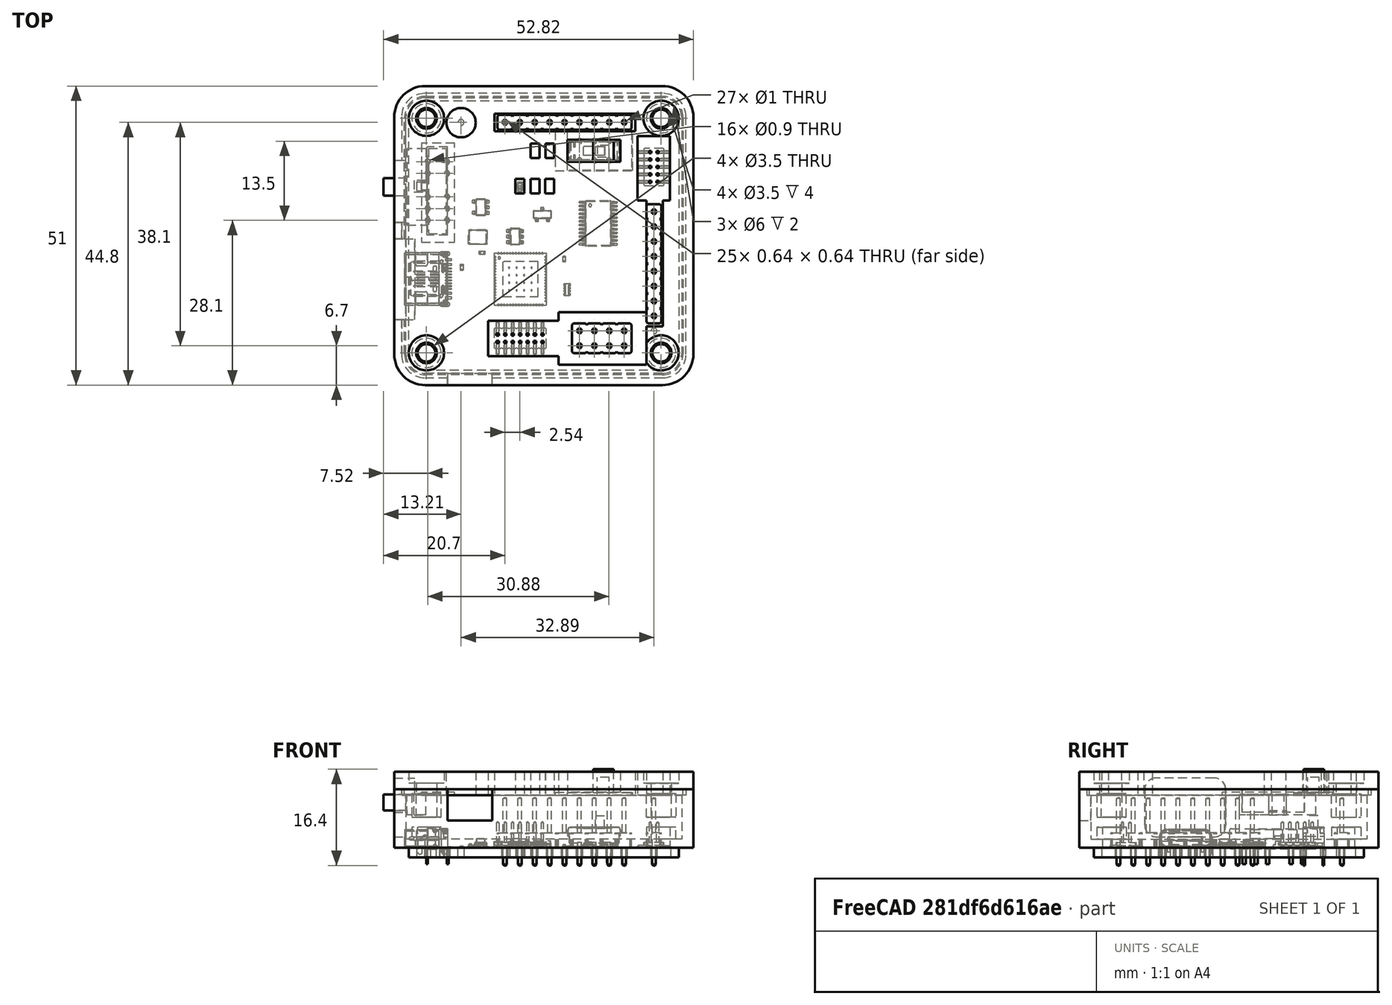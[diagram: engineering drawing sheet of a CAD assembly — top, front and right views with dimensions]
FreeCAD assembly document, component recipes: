
FREECAD ASSEMBLY — COMPONENT RECIPES ("TigarDen")

This assembly document has 73 components, labeled P0..P72 below (a component is one placed body or linked part). 11 of them carry a construction recipe — the FreeCAD feature program that regenerates the part from scratch, quoted from this document or its linked companion documents; the rest are supplied as boundary geometry only. No exploded tour is included for this assembly.
COMPONENT P0 — recipe-attached ("Body", modeled in this document).
Construction recipe (the document's own serialized feature program — sketch geometry with constraints, then the solid features built on it; lengths are millimeters unless a unit is written):

FEATURE [Sketcher::SketchObject] Sketch  label="Tikgard Sketch"
  AttachmentOffset = pos=(0,0,6) rot=(0,0,1;0rad)
  FullyConstrained = true
  MapMode = 5
  Placement = pos=(0,0,6) rot=(0,0,1;0rad)
  Support = -> [XY_Plane]
  sketch-geometry (8):
    g0: LineSegment StartX=-20.2 StartY=23.5 StartZ=0 EndX=20.2 EndY=23.5 EndZ=0
    g1: LineSegment StartX=23.5 StartY=20.2 StartZ=0 EndX=23.5 EndY=-20.2 EndZ=0
    g2: LineSegment StartX=20.2 StartY=-23.5 StartZ=0 EndX=-20.2 EndY=-23.5 EndZ=0
    g3: LineSegment StartX=-23.5 StartY=-20.2 StartZ=0 EndX=-23.5 EndY=20.2 EndZ=0
    g4: ArcOfCircle CenterX=-20.2 CenterY=20.2 CenterZ=0 NormalX=0 NormalY=0 NormalZ=1 AngleXU=0 Radius=3.3 StartAngle=1.5708 EndAngle=3.14159
    g5: ArcOfCircle CenterX=20.2 CenterY=20.2 CenterZ=0 NormalX=0 NormalY=0 NormalZ=1 AngleXU=0 Radius=3.3 StartAngle=0 EndAngle=1.5708
    g6: ArcOfCircle CenterX=20.2 CenterY=-20.2 CenterZ=0 NormalX=0 NormalY=0 NormalZ=1 AngleXU=0 Radius=3.3 StartAngle=4.71239 EndAngle=6.28319
    g7: ArcOfCircle CenterX=-20.2 CenterY=-20.2 CenterZ=0 NormalX=0 NormalY=0 NormalZ=1 AngleXU=0 Radius=3.3 StartAngle=3.14159 EndAngle=4.71239
  constraints (20):
    c: Horizontal(g0)
    c: Horizontal(g2)
    c: Vertical(g1)
    c: Vertical(g3)
    c: Distance(g-1,g2) = 23.5
    c: Distance(g-1,g3) = 23.5
    c: Tangent(g0,g4) = 1.5708
    c: Tangent(g3,g4) = 1.5708
    c: Tangent(g0,g5) = 1.5708
    c: Tangent(g1,g5) = 1.5708
    c: Tangent(g1,g6) = 1.5708
    c: Tangent(g2,g6) = 1.5708
    c: Tangent(g2,g7) = 1.5708
    c: Tangent(g3,g7) = 1.5708
    c: Radius(g4) = 3.3
    c: Radius(g6) = 3.3
    c: Radius(g7) = 3.3
    c: Distance(g3,g1) = 47
    c: Distance(g0,g2) = 47
    c: Radius(g5) = 3.3
FEATURE [Sketcher::SketchObject] Sketch001  label="Out Wall Sketch"
  FullyConstrained = true
  MapMode = 5
  Support = -> [XY_Plane]
  sketch-geometry (8):
    g0: LineSegment StartX=-20.2 StartY=25.5 StartZ=0 EndX=20.2 EndY=25.5 EndZ=0
    g1: LineSegment StartX=25.5 StartY=20.2 StartZ=0 EndX=25.5 EndY=-20.2 EndZ=0
    g2: LineSegment StartX=20.2 StartY=-25.5 StartZ=0 EndX=-20.2 EndY=-25.5 EndZ=0
    g3: LineSegment StartX=-25.5 StartY=-20.2 StartZ=0 EndX=-25.5 EndY=20.2 EndZ=0
    g4: ArcOfCircle CenterX=-20.2 CenterY=20.2 CenterZ=0 NormalX=0 NormalY=0 NormalZ=1 AngleXU=0 Radius=5.3 StartAngle=1.5708 EndAngle=3.14159
    g5: ArcOfCircle CenterX=-20.2 CenterY=-20.2 CenterZ=0 NormalX=0 NormalY=0 NormalZ=1 AngleXU=0 Radius=5.3 StartAngle=3.14159 EndAngle=4.71239
    g6: ArcOfCircle CenterX=20.2 CenterY=-20.2 CenterZ=0 NormalX=0 NormalY=0 NormalZ=1 AngleXU=0 Radius=5.3 StartAngle=4.71239 EndAngle=6.28319
    g7: ArcOfCircle CenterX=20.2 CenterY=20.2 CenterZ=0 NormalX=0 NormalY=0 NormalZ=1 AngleXU=0 Radius=5.3 StartAngle=1e-16 EndAngle=1.5708
  constraints (20):
    c: Horizontal(g0)
    c: Horizontal(g2)
    c: Vertical(g1)
    c: Vertical(g3)
    c: Tangent(g0,g4) = 1.5708
    c: Tangent(g3,g4) = 1.5708
    c: Tangent(g3,g5) = 1.5708
    c: Tangent(g2,g5) = 1.5708
    c: Tangent(g2,g6) = 1.5708
    c: Tangent(g1,g6) = 1.5708
    c: Tangent(g0,g7) = 1.5708
    c: Tangent(g1,g7) = 1.5708
    c: Radius(g4) = 5.3
    c: Radius(g7) = 5.3
    c: Radius(g6) = 5.3
    c: Radius(g5) = 5.3
    c: Distance(g0,g2) = 51
    c: Distance(g3,g1) = 51
    c: Distance(g-1,g0) = 25.5
    c: Distance(g-1,g1) = 25.5
FEATURE [PartDesign::Pad] Pad  label="Base"
  Direction = (1,1,1)
  Length = 10
  Length2 = 100
  Profile = -> Sketch001
  Type = 0
FEATURE [PartDesign::Pocket] Pocket  label="Tigard Cutout"
  BaseFeature = -> Pad
  Length = 9
  Length2 = 100
  Midplane = true
  Profile = -> Sketch
  Type = 0
FEATURE [Sketcher::SketchObject] Sketch002  label="Standoff Sketch"
  FullyConstrained = true
  MapMode = 5
  Placement = pos=(0,0,1.5) rot=(0,0,1;0rad)
  Support = -> [Pocket]
  sketch-geometry (4):
    g0: Circle CenterX=-20 CenterY=20 CenterZ=0 NormalX=0 NormalY=0 NormalZ=1 AngleXU=0 Radius=2.5
    g1: Circle CenterX=20 CenterY=20 CenterZ=0 NormalX=0 NormalY=0 NormalZ=1 AngleXU=0 Radius=2.5
    g2: Circle CenterX=20 CenterY=-20 CenterZ=0 NormalX=0 NormalY=0 NormalZ=1 AngleXU=0 Radius=2.5
    g3: Circle CenterX=-20 CenterY=-20 CenterZ=0 NormalX=0 NormalY=0 NormalZ=1 AngleXU=0 Radius=2.5
  constraints (12):
    c: Distance(g0,g-2) = 20
    c: Distance(g0,g-1) = 20
    c: Radius(g0) = 2.5
    c: Equal(g0,g1)
    c: Equal(g0,g3)
    c: Equal(g1,g2)
    c: DistanceX(g-2,g1) = 20
    c: DistanceY(g-1,g1) = 20
    c: DistanceY(g-1,g2) = -20
    c: DistanceX(g-2,g2) = 20
    c: DistanceX(g-2,g3) = -20
    c: DistanceY(g-1,g3) = -20
FEATURE [Sketcher::SketchObject] Sketch003  label="Screw Holes Sketch"
  FullyConstrained = true
  MapMode = 5
  Placement = pos=(0,0,3.5) rot=(0,0,1;0rad)
  sketch-geometry (4):
    g0: Circle CenterX=-20 CenterY=20 CenterZ=0 NormalX=0 NormalY=0 NormalZ=1 AngleXU=0 Radius=1.5
    g1: Circle CenterX=20 CenterY=20 CenterZ=0 NormalX=0 NormalY=0 NormalZ=1 AngleXU=0 Radius=1.5
    g2: Circle CenterX=20 CenterY=-20 CenterZ=0 NormalX=0 NormalY=0 NormalZ=1 AngleXU=0 Radius=1.5
    g3: Circle CenterX=-20 CenterY=-20 CenterZ=0 NormalX=0 NormalY=0 NormalZ=1 AngleXU=0 Radius=1.5
  constraints (12):
    c: DistanceX(g-2,g0) = -20
    c: Distance(g0,g-1) = 20
    c: Radius(g0) = 1.5
    c: Equal(g0,g1)
    c: Equal(g0,g2)
    c: Equal(g3,g2)
    c: Distance(g3,g-1) = 20
    c: Distance(g3,g-2) = 20
    c: Distance(g2,g-2) = 20
    c: Distance(g2,g-1) = 20
    c: Distance(g1,g-2) = 20
    c: Distance(g1,g-1) = 20
FEATURE [Sketcher::SketchObject] Sketch004  label="Base Ridge Sketch"
  FullyConstrained = true
  MapMode = 5
  Placement = pos=(0,0,10) rot=(0,0,1;0rad)
  Support = -> [Pocket]
  sketch-geometry (8):
    g0: LineSegment StartX=-20.25 StartY=24.25 StartZ=0 EndX=20.25 EndY=24.25 EndZ=0
    g1: LineSegment StartX=24.25 StartY=20.25 StartZ=0 EndX=24.25 EndY=-20.25 EndZ=0
    g2: LineSegment StartX=20.25 StartY=-24.25 StartZ=0 EndX=-20.25 EndY=-24.25 EndZ=0
    g3: LineSegment StartX=-24.25 StartY=-20.25 StartZ=0 EndX=-24.25 EndY=20.25 EndZ=0
    g4: ArcOfCircle CenterX=-20.25 CenterY=20.25 CenterZ=0 NormalX=0 NormalY=0 NormalZ=1 AngleXU=0 Radius=4 StartAngle=1.5708 EndAngle=3.14159
    g5: ArcOfCircle CenterX=20.25 CenterY=20.25 CenterZ=0 NormalX=0 NormalY=0 NormalZ=1 AngleXU=0 Radius=4 StartAngle=0 EndAngle=1.5708
    g6: ArcOfCircle CenterX=20.25 CenterY=-20.25 CenterZ=0 NormalX=0 NormalY=0 NormalZ=1 AngleXU=0 Radius=4 StartAngle=4.71239 EndAngle=6.28319
    g7: ArcOfCircle CenterX=-20.25 CenterY=-20.25 CenterZ=0 NormalX=0 NormalY=0 NormalZ=1 AngleXU=0 Radius=4 StartAngle=3.14159 EndAngle=4.71239
  constraints (20):
    c: Horizontal(g0)
    c: Horizontal(g2)
    c: Vertical(g1)
    c: Vertical(g3)
    c: Distance(g-1,g2) = 24.25
    c: Distance(g-1,g1) = 24.25
    c: Distance(g-1,g0) = 24.25
    c: Distance(g-1,g3) = 24.25
    c: Tangent(g0,g4) = 1.5708
    c: Tangent(g3,g4) = 1.5708
    c: Tangent(g0,g5) = 1.5708
    c: Tangent(g1,g5) = 1.5708
    c: Tangent(g1,g6) = 1.5708
    c: Tangent(g2,g6) = 1.5708
    c: Tangent(g2,g7) = 1.5708
    c: Tangent(g3,g7) = 1.5708
    c: Radius(g4) = 4
    c: Equal(g4,g5)
    c: Equal(g6,g4)
    c: Equal(g7,g4)
FEATURE [PartDesign::Pocket] Pocket001  label="Base Ridge"
  BaseFeature = -> Pocket
  Length = 2
  Length2 = 100
  Midplane = true
  Profile = -> Sketch004
  Type = 0
FEATURE [PartDesign::Pad] Pad004  label="Standoff"
  BaseFeature = -> Pocket001
  Direction = (1,1,1)
  Length = 2
  Length2 = 100
  Profile = -> Sketch002
  Type = 0
FEATURE [PartDesign::Pocket] Pocket002  label="Screw Holes"
  BaseFeature = -> Pad004
  Length = 5
  Length2 = 100
  Profile = -> Sketch003
  Type = 1
FEATURE [PartDesign::Body] Body
  Group = -> [Sketch,Sketch001,Pad,Pocket,Sketch002,Sketch003,Sketch004,Pocket001,Pad004,Pocket002]
  Origin = -> Origin
  Tip = -> Pocket002
COMPONENT P1 — recipe-attached ("Top", modeled in this document).
Construction recipe (the document's own serialized feature program — sketch geometry with constraints, then the solid features built on it; lengths are millimeters unless a unit is written):

FEATURE [Sketcher::SketchObject] Sketch005  label="Lid Inset Sketch"
  AttachmentOffset = pos=(0,0,7) rot=(0,0,1;0rad)
  FullyConstrained = true
  MapMode = 5
  Placement = pos=(0,0,7) rot=(0,0,1;0rad)
  Support = -> [XY_Plane001]
  sketch-geometry (8):
    g0: LineSegment StartX=-20.15 StartY=23.75 StartZ=0 EndX=20.15 EndY=23.75 EndZ=0
    g1: LineSegment StartX=23.75 StartY=20.15 StartZ=0 EndX=23.75 EndY=-20.15 EndZ=0
    g2: LineSegment StartX=20.15 StartY=-23.75 StartZ=0 EndX=-20.15 EndY=-23.75 EndZ=0
    g3: LineSegment StartX=-23.75 StartY=-20.15 StartZ=0 EndX=-23.75 EndY=20.15 EndZ=0
    g4: ArcOfCircle CenterX=-20.15 CenterY=20.15 CenterZ=0 NormalX=0 NormalY=0 NormalZ=1 AngleXU=0 Radius=3.6 StartAngle=1.5708 EndAngle=3.14159
    g5: ArcOfCircle CenterX=20.15 CenterY=20.15 CenterZ=0 NormalX=0 NormalY=0 NormalZ=1 AngleXU=0 Radius=3.6 StartAngle=2e-16 EndAngle=1.5708
    g6: ArcOfCircle CenterX=20.15 CenterY=-20.15 CenterZ=0 NormalX=0 NormalY=0 NormalZ=1 AngleXU=0 Radius=3.6 StartAngle=4.71239 EndAngle=6.28319
    g7: ArcOfCircle CenterX=-20.15 CenterY=-20.15 CenterZ=0 NormalX=0 NormalY=0 NormalZ=1 AngleXU=0 Radius=3.6 StartAngle=3.14159 EndAngle=4.71239
  constraints (20):
    c: Horizontal(g0)
    c: Horizontal(g2)
    c: Vertical(g1)
    c: Vertical(g3)
    c: Distance(g-1,g0) = 23.75
    c: Distance(g-1,g2) = 23.75
    c: Distance(g-1,g1) = 23.75
    c: Distance(g-1,g3) = 23.75
    c: Tangent(g0,g4) = 1.5708
    c: Tangent(g3,g4) = 1.5708
    c: Tangent(g0,g5) = 1.5708
    c: Tangent(g1,g5) = 1.5708
    c: Tangent(g1,g6) = 1.5708
    c: Tangent(g2,g6) = 1.5708
    c: Tangent(g2,g7) = 1.5708
    c: Tangent(g3,g7) = 1.5708
    c: Radius(g4) = 3.6
    c: Equal(g4,g5)
    c: Equal(g6,g4)
    c: Equal(g4,g7)
FEATURE [PartDesign::Pad] Pad002  label="Lid Inset"
  Direction = (1,1,1)
  Length = 1
  Length2 = 100
  Profile = -> Sketch005
  Type = 0
FEATURE [Sketcher::SketchObject] Sketch006  label="Lid Sketch"
  FullyConstrained = true
  MapMode = 5
  Placement = pos=(0,0,8) rot=(0,0,1;0rad)
  Support = -> [Pad002]
  sketch-geometry (8):
    g0: LineSegment StartX=-20.2 StartY=25.5 StartZ=0 EndX=20.2 EndY=25.5 EndZ=0
    g1: LineSegment StartX=25.5 StartY=20.2 StartZ=0 EndX=25.5 EndY=-20.2 EndZ=0
    g2: LineSegment StartX=20.2 StartY=-25.5 StartZ=0 EndX=-20.2 EndY=-25.5 EndZ=0
    g3: LineSegment StartX=-25.5 StartY=-20.2 StartZ=0 EndX=-25.5 EndY=20.2 EndZ=0
    g4: ArcOfCircle CenterX=-20.2 CenterY=20.2 CenterZ=0 NormalX=0 NormalY=0 NormalZ=1 AngleXU=0 Radius=5.3 StartAngle=1.5708 EndAngle=3.14159
    g5: ArcOfCircle CenterX=20.2 CenterY=20.2 CenterZ=0 NormalX=0 NormalY=0 NormalZ=1 AngleXU=0 Radius=5.3 StartAngle=1e-16 EndAngle=1.5708
    g6: ArcOfCircle CenterX=20.2 CenterY=-20.2 CenterZ=0 NormalX=0 NormalY=0 NormalZ=1 AngleXU=0 Radius=5.3 StartAngle=4.71239 EndAngle=6.28319
    g7: ArcOfCircle CenterX=-20.2 CenterY=-20.2 CenterZ=0 NormalX=0 NormalY=0 NormalZ=1 AngleXU=0 Radius=5.3 StartAngle=3.14159 EndAngle=4.71239
  constraints (20):
    c: Horizontal(g0)
    c: Horizontal(g2)
    c: Vertical(g1)
    c: Vertical(g3)
    c: Distance(g-1,g0) = 25.5
    c: Distance(g-1,g1) = 25.5
    c: Distance(g-1,g2) = 25.5
    c: Distance(g-1,g3) = 25.5
    c: Tangent(g0,g4) = 1.5708
    c: Tangent(g3,g4) = 1.5708
    c: Radius(g4) = 5.3
    c: Tangent(g0,g5) = 1.5708
    c: Tangent(g1,g5) = 1.5708
    c: Tangent(g1,g6) = 1.5708
    c: Tangent(g2,g6) = 1.5708
    c: Tangent(g2,g7) = 1.5708
    c: Tangent(g3,g7) = 1.5708
    c: Equal(g4,g5)
    c: Equal(g4,g6)
    c: Equal(g4,g7)
FEATURE [PartDesign::Pad] Pad003  label="Lid"
  BaseFeature = -> Pad002
  Direction = (1,1,1)
  Length = 3
  Length2 = 100
  Profile = -> Sketch006
  Type = 0
FEATURE [Sketcher::SketchObject] Sketch007  label="Screw Holes Lid"
  FullyConstrained = true
  MapMode = 5
  Placement = pos=(0,0,11) rot=(0,0,1;0rad)
  Support = -> [Pad003]
  sketch-geometry (4):
    g0: Circle CenterX=-20 CenterY=20 CenterZ=0 NormalX=0 NormalY=0 NormalZ=1 AngleXU=0 Radius=1.5
    g1: Circle CenterX=20 CenterY=20 CenterZ=0 NormalX=0 NormalY=0 NormalZ=1 AngleXU=0 Radius=1.5
    g2: Circle CenterX=20 CenterY=-20 CenterZ=0 NormalX=0 NormalY=0 NormalZ=1 AngleXU=0 Radius=1.5
    g3: Circle CenterX=-20 CenterY=-20 CenterZ=0 NormalX=0 NormalY=0 NormalZ=1 AngleXU=0 Radius=1.5
  constraints (12):
    c: Radius(g0) = 1.5
    c: DistanceX(g-2,g0) = -20
    c: DistanceY(g-1,g0) = 20
    c: Equal(g0,g1)
    c: Equal(g0,g2)
    c: Equal(g0,g3)
    c: DistanceX(g-2,g1) = 20
    c: DistanceY(g-1,g1) = 20
    c: DistanceX(g-2,g2) = 20
    c: DistanceY(g-1,g2) = -20
    c: DistanceX(g-2,g3) = -20
    c: DistanceY(g-1,g3) = -20
FEATURE [PartDesign::Hole] Hole
  BaseFeature = -> Pad003
  Depth = 25
  DepthType = 1
  Diameter = 3.5
  DrillForDepth = true
  DrillPoint = 1
  DrillPointAngle = 118
  HoleCutCountersinkAngle = 90
  HoleCutCustomValues = false
  HoleCutDepth = 2
  HoleCutDiameter = 6
  HoleCutType = 1
  ModelActualThread = false
  Profile = -> Sketch007
  Tapered = false
  TaperedAngle = 90
  ThreadAngle = 0
  ThreadClass = 0
  ThreadCutOffInner = 0
  ThreadCutOffOuter = 0
  ThreadDirection = 0
  ThreadFit = 0
  ThreadPitch = 0
  ThreadSize = 0
  ThreadType = 0
  Threaded = false
FEATURE [PartDesign::Body] Body001  label="Top"
  Group = -> [Sketch005,Pad002,Sketch006,Pad003,Sketch007,Hole]
  Origin = -> Origin001
  Placement = pos=(0,0,2) rot=(0,0,1;0rad)
  Tip = -> Hole
COMPONENT P2 — recipe-attached ("USB-C Cutter", modeled in this document).
Construction recipe (the document's own serialized feature program — sketch geometry with constraints, then the solid features built on it; lengths are millimeters unless a unit is written):

FEATURE [Sketcher::SketchObject] Sketch008
  FullyConstrained = false
  MapMode = 5
  Placement = pos=(0,0,0) rot=(-0.57735,0.57735,0.57735;4.18879rad)
  Support = -> [YZ_Plane002]
  sketch-geometry (8):
    g0: LineSegment StartX=2.5358 StartY=11.912 StartZ=0 EndX=12.3476 EndY=11.912 EndZ=0
    g1: LineSegment StartX=14.3476 StartY=9.91198 StartZ=0 EndX=14.3476 EndY=3.8669 EndZ=0
    g2: LineSegment StartX=12.3476 StartY=1.8669 StartZ=0 EndX=2.5358 EndY=1.8669 EndZ=0
    g3: LineSegment StartX=0.535801 StartY=3.8669 StartZ=0 EndX=0.535801 EndY=9.91198 EndZ=0
    g4: ArcOfCircle CenterX=2.5358 CenterY=9.91198 CenterZ=0 NormalX=0 NormalY=0 NormalZ=1 AngleXU=0 Radius=2 StartAngle=1.5708 EndAngle=3.14159
    g5: ArcOfCircle CenterX=12.3476 CenterY=9.91198 CenterZ=0 NormalX=0 NormalY=0 NormalZ=1 AngleXU=0 Radius=2 StartAngle=0 EndAngle=1.5708
    g6: ArcOfCircle CenterX=12.3476 CenterY=3.8669 CenterZ=0 NormalX=0 NormalY=0 NormalZ=1 AngleXU=0 Radius=2 StartAngle=4.71239 EndAngle=6.28319
    g7: ArcOfCircle CenterX=2.5358 CenterY=3.8669 CenterZ=0 NormalX=0 NormalY=0 NormalZ=1 AngleXU=0 Radius=2 StartAngle=3.14159 EndAngle=4.71239
  constraints (16):
    c: Horizontal(g0)
    c: Horizontal(g2)
    c: Vertical(g1)
    c: Vertical(g3)
    c: Tangent(g3,g4) = 1.5708
    c: Tangent(g0,g4) = 1.5708
    c: Tangent(g0,g5) = 1.5708
    c: Tangent(g1,g5) = 1.5708
    c: Tangent(g1,g6) = 1.5708
    c: Tangent(g2,g6) = 1.5708
    c: Tangent(g2,g7) = 1.5708
    c: Tangent(g3,g7) = 1.5708
    c: Radius(g4) = 2
    c: Equal(g4,g5)
    c: Equal(g4,g7)
    c: Equal(g4,g6)
FEATURE [PartDesign::Pad] Pad005
  Direction = (1,1,1)
  Length = 4
  Length2 = 100
  Placement = pos=(0,0,0) rot=(0.57735,0.57735,0.57735;2.0944rad)
  Profile = -> Sketch008
  Reversed = true
  Type = 0
FEATURE [PartDesign::Body] Body002  label="USB-C Cutter"
  Group = -> [Sketch008,Pad005]
  Origin = -> Origin002
  Placement = pos=(-26,0,0) rot=(0,0,1;0rad)
  Tip = -> Pad005
COMPONENT P3 — recipe-attached ("Body Pocketed", modeled in this document).
Construction recipe (the document's own serialized feature program — sketch geometry with constraints, then the solid features built on it; lengths are millimeters unless a unit is written):

FEATURE [PartDesign::FeatureBase] BaseFeature
  BaseFeature = -> Cut001
FEATURE [Sketcher::SketchObject] Sketch009  label="Voltage Switch Cutout Sketch"
  FullyConstrained = false
  MapMode = 5
  Placement = pos=(-25.5,0,0) rot=(0.57735,-0.57735,-0.57735;2.0944rad)
  Support = -> [BaseFeature]
  sketch-geometry (4):
    g0: LineSegment StartX=-12.842 StartY=6.08226 StartZ=0 EndX=-2.23477 EndY=6.08226 EndZ=0
    g1: LineSegment StartX=-2.23477 StartY=6.08226 StartZ=0 EndX=-2.23477 EndY=10.517 EndZ=0
    g2: LineSegment StartX=-2.23477 StartY=10.517 StartZ=0 EndX=-12.842 EndY=10.517 EndZ=0
    g3: LineSegment StartX=-12.842 StartY=10.517 StartZ=0 EndX=-12.842 EndY=6.08226 EndZ=0
  constraints (8):
    c: Coincident(g0,g1)
    c: Coincident(g1,g2)
    c: Coincident(g2,g3)
    c: Coincident(g3,g0)
    c: Horizontal(g0)
    c: Horizontal(g2)
    c: Vertical(g1)
    c: Vertical(g3)
FEATURE [PartDesign::Pocket] Pocket003  label="Voltage Switch Cutout"
  BaseFeature = -> BaseFeature
  Length = 5
  Length2 = 100
  Placement = pos=(0,0,-40) rot=(0,0,1;0rad)
  Profile = -> Sketch009
  Type = 0
FEATURE [Sketcher::SketchObject] Sketch010  label="I2C Cutout Sketch"
  FullyConstrained = false
  MapMode = 5
  Placement = pos=(0,-25.5,0) rot=(1,0,0;1.5708rad)
  Support = -> [Pocket003]
  sketch-geometry (4):
    g0: LineSegment StartX=-8.76633 StartY=4.68576 StartZ=0 EndX=-16.4093 EndY=4.68576 EndZ=0
    g1: LineSegment StartX=-16.4093 StartY=4.68576 StartZ=0 EndX=-16.4093 EndY=10.0143 EndZ=0
    g2: LineSegment StartX=-16.4093 StartY=10.0143 StartZ=0 EndX=-8.76633 EndY=10.0143 EndZ=0
    g3: LineSegment StartX=-8.76633 StartY=10.0143 StartZ=0 EndX=-8.76633 EndY=4.68576 EndZ=0
  constraints (8):
    c: Coincident(g0,g1)
    c: Coincident(g1,g2)
    c: Coincident(g2,g3)
    c: Coincident(g3,g0)
    c: Horizontal(g0)
    c: Horizontal(g2)
    c: Vertical(g1)
    c: Vertical(g3)
FEATURE [PartDesign::Pocket] Pocket004  label="I2C Cutout"
  BaseFeature = -> Pocket003
  Length = 5
  Length2 = 100
  Profile = -> Sketch010
  Type = 0
FEATURE [PartDesign::Body] Body003  label="Body Pocketed"
  BaseFeature = -> Cut001
  Group = -> [BaseFeature,Sketch009,Pocket003,Sketch010,Pocket004]
  Origin = -> Origin003
  Tip = -> Pocket004
COMPONENT P4 — recipe-attached ("Lid Pocketed", modeled in this document).
Construction recipe (the document's own serialized feature program — sketch geometry with constraints, then the solid features built on it; lengths are millimeters unless a unit is written):

FEATURE [PartDesign::FeatureBase] BaseFeature001
  BaseFeature = -> Cut
FEATURE [Sketcher::SketchObject] Sketch011  label="Lid Cutout Sketch"
  FullyConstrained = false
  MapMode = 5
  Placement = pos=(0,0,13) rot=(0,0,1;0rad)
  Support = -> [BaseFeature001]
  sketch-geometry (45):
    g0: LineSegment StartX=4.02651 StartY=16.3347 StartZ=0 EndX=13.0689 EndY=16.3347 EndZ=0
    g1: LineSegment StartX=13.0689 StartY=16.3347 StartZ=0 EndX=13.0689 EndY=12.5671 EndZ=0
    g2: LineSegment StartX=13.0689 StartY=12.5671 StartZ=0 EndX=4.02651 EndY=12.5671 EndZ=0
    g3: LineSegment StartX=4.02651 StartY=12.5671 StartZ=0 EndX=4.02651 EndY=16.3347 EndZ=0
    g4: LineSegment StartX=15.9986 StartY=16.9943 StartZ=0 EndX=21.4986 EndY=16.9943 EndZ=0
    g5: LineSegment StartX=21.4986 StartY=16.9943 StartZ=0 EndX=21.4986 EndY=5.99431 EndZ=0
    g6: LineSegment StartX=15.9986 StartY=5.99431 StartZ=0 EndX=15.9986 EndY=16.9943 EndZ=0
    g7: LineSegment StartX=20.2805 StartY=5.99431 StartZ=0 EndX=20.2805 EndY=-15.5057 EndZ=0
    g8: LineSegment StartX=20.2805 StartY=-15.5057 StartZ=0 EndX=17.5 EndY=-15.5057 EndZ=0
    g9: LineSegment StartX=17.5 StartY=-13.0474 StartZ=0 EndX=17.5 EndY=5.99431 EndZ=0
    g10: LineSegment StartX=-8.41441 StartY=20.8038 StartZ=0 EndX=15.5856 EndY=20.8038 EndZ=0
    g11: LineSegment StartX=15.5856 StartY=20.8038 StartZ=0 EndX=15.5856 EndY=17.8038 EndZ=0
    g12: LineSegment StartX=15.5856 StartY=17.8038 StartZ=0 EndX=-8.41441 EndY=17.8038 EndZ=0
    g13: LineSegment StartX=-8.41441 StartY=17.8038 StartZ=0 EndX=-8.41441 EndY=20.8038 EndZ=0
    g14: LineSegment StartX=15.9986 StartY=5.99431 StartZ=0 EndX=17.5 EndY=5.99431 EndZ=0
    g15: LineSegment StartX=20.2805 StartY=5.99431 StartZ=0 EndX=21.4986 EndY=5.99431 EndZ=0
    g16: LineSegment StartX=-2.2549 StartY=15.7 StartZ=0 EndX=-0.754905 EndY=15.7 EndZ=0
    g17: LineSegment StartX=-0.754905 StartY=15.7 StartZ=0 EndX=-0.754905 EndY=13.2 EndZ=0
    g18: LineSegment StartX=-0.754905 StartY=13.2 StartZ=0 EndX=-2.2549 EndY=13.2 EndZ=0
    g19: LineSegment StartX=-2.2549 StartY=13.2 StartZ=0 EndX=-2.2549 EndY=15.7 EndZ=0
    g20: LineSegment StartX=0.270606 StartY=15.7 StartZ=0 EndX=1.77061 EndY=15.7 EndZ=0
    g21: LineSegment StartX=1.77061 StartY=15.7 StartZ=0 EndX=1.77061 EndY=13.2 EndZ=0
    g22: LineSegment StartX=1.77061 StartY=13.2 StartZ=0 EndX=0.270606 EndY=13.2 EndZ=0
    g23: LineSegment StartX=0.270606 StartY=13.2 StartZ=0 EndX=0.270606 EndY=15.7 EndZ=0
    g24: LineSegment StartX=0.239071 StartY=9.7 StartZ=0 EndX=1.73907 EndY=9.7 EndZ=0
    g25: LineSegment StartX=1.73907 StartY=9.7 StartZ=0 EndX=1.73907 EndY=7.2 EndZ=0
    g26: LineSegment StartX=1.73907 StartY=7.2 StartZ=0 EndX=0.239071 EndY=7.2 EndZ=0
    g27: LineSegment StartX=0.239071 StartY=7.2 StartZ=0 EndX=0.239071 EndY=9.7 EndZ=0
    g28: LineSegment StartX=-2.24916 StartY=9.7 StartZ=0 EndX=-0.749158 EndY=9.7 EndZ=0
    g29: LineSegment StartX=-0.749158 StartY=9.7 StartZ=0 EndX=-0.749158 EndY=7.2 EndZ=0
    g30: LineSegment StartX=-0.749158 StartY=7.2 StartZ=0 EndX=-2.24916 EndY=7.2 EndZ=0
    g31: LineSegment StartX=-2.24916 StartY=7.2 StartZ=0 EndX=-2.24916 EndY=9.7 EndZ=0
    g32: LineSegment StartX=-4.81914 StartY=9.7 StartZ=0 EndX=-3.31914 EndY=9.7 EndZ=0
    g33: LineSegment StartX=-3.31914 StartY=9.7 StartZ=0 EndX=-3.31914 EndY=7.2 EndZ=0
    g34: LineSegment StartX=-3.31914 StartY=7.2 StartZ=0 EndX=-4.81914 EndY=7.2 EndZ=0
    g35: LineSegment StartX=-4.81914 StartY=7.2 StartZ=0 EndX=-4.81914 EndY=9.7 EndZ=0
    g36: LineSegment StartX=-9.5 StartY=-14.5357 StartZ=0 EndX=2.5 EndY=-14.5357 EndZ=0
    g37: LineSegment StartX=2.5 StartY=-20.5357 StartZ=0 EndX=-9.5 EndY=-20.5357 EndZ=0
    g38: LineSegment StartX=-9.5 StartY=-20.5357 StartZ=0 EndX=-9.5 EndY=-14.5357 EndZ=0
    g39: LineSegment StartX=2.5 StartY=-13.0474 StartZ=0 EndX=17.5 EndY=-13.0474 EndZ=0
    g40: LineSegment StartX=17.5 StartY=-15.5057 StartZ=0 EndX=17.5 EndY=-22.0474 EndZ=0
    g41: LineSegment StartX=17.5 StartY=-22.0474 StartZ=0 EndX=2.5 EndY=-22.0474 EndZ=0
    g42: LineSegment StartX=2.5 StartY=-22.0474 StartZ=0 EndX=2.5 EndY=-20.5357 EndZ=0
    g43: LineSegment StartX=2.5 StartY=-14.5357 StartZ=0 EndX=2.5 EndY=-13.0474 EndZ=0
    g44: Circle CenterX=-14.1023 CenterY=19.26 CenterZ=0 NormalX=0 NormalY=0 NormalZ=1 AngleXU=0 Radius=2.5
  constraints (115):
    c: Coincident(g0,g1)
    c: Coincident(g1,g2)
    c: Coincident(g2,g3)
    c: Coincident(g3,g0)
    c: Horizontal(g0)
    c: Horizontal(g2)
    c: Vertical(g1)
    c: Vertical(g3)
    c: Coincident(g4,g5)
    c: Coincident(g6,g4)
    c: Horizontal(g4)
    c: Vertical(g5)
    c: Vertical(g6)
    c: Coincident(g7,g8)
    c: Horizontal(g8)
    c: Vertical(g7)
    c: Vertical(g9)
    c: Distance(g7) = 21.5
    c: Coincident(g10,g11)
    c: Coincident(g11,g12)
    c: Coincident(g12,g13)
    c: Coincident(g13,g10)
    c: Horizontal(g10)
    c: Horizontal(g12)
    c: Vertical(g11)
    c: Vertical(g13)
    c: Distance(g10) = 24
    c: Distance(g13) = 3
    c: Distance(g4) = 5.5
    c: Coincident(g14,g6)
    c: Coincident(g14,g9)
    c: Horizontal(g14)
    c: Coincident(g15,g7)
    c: Coincident(g15,g5)
    c: Horizontal(g15)
    c: Distance(g5) = 11
    c: Equal(g5,g6)
    c: Coincident(g16,g17)
    c: Coincident(g17,g18)
    c: Coincident(g18,g19)
    c: Coincident(g19,g16)
    c: Horizontal(g16)
    c: Horizontal(g18)
    c: Vertical(g17)
    c: Vertical(g19)
    c: Coincident(g20,g21)
    c: Coincident(g21,g22)
    c: Coincident(g22,g23)
    c: Coincident(g23,g20)
    c: Horizontal(g20)
    c: Horizontal(g22)
    c: Vertical(g21)
    c: Vertical(g23)
    c: Coincident(g24,g25)
    c: Coincident(g25,g26)
    c: Coincident(g26,g27)
    c: Coincident(g27,g24)
    c: Horizontal(g24)
    c: Horizontal(g26)
    c: Vertical(g25)
    c: Vertical(g27)
    c: Coincident(g28,g29)
    c: Coincident(g29,g30)
    c: Coincident(g30,g31)
    c: Coincident(g31,g28)
    c: Horizontal(g28)
    c: Horizontal(g30)
    c: Vertical(g29)
    c: Vertical(g31)
    c: Coincident(g32,g33)
    c: Coincident(g33,g34)
    c: Coincident(g34,g35)
    c: Coincident(g35,g32)
    c: Horizontal(g32)
    c: Horizontal(g34)
    c: Vertical(g33)
    c: Vertical(g35)
    c: Coincident(g37,g38)
    c: Coincident(g38,g36)
    c: Horizontal(g36)
    c: Horizontal(g37)
    c: Vertical(g38)
    c: Distance(g36) = 12
    c: Distance(g38) = 6
    c: Coincident(g40,g41)
    c: Coincident(g41,g42)
    c: Coincident(g43,g39)
    c: Horizontal(g39)
    c: Horizontal(g41)
    c: Vertical(g40)
    c: Vertical(g42)
    c: Distance(g39) = 15
    c: Coincident(g42,g37)
    c: Coincident(g43,g36)
    c: Tangent(g42,g43)
    c: Distance(g19) = 2.5
    c: Distance(g16) = 1.5
    c: Equal(g19,g23)
    c: Equal(g16,g20)
    c: Equal(g16,g28)
    c: Equal(g19,g31)
    c: Equal(g31,g27)
    c: Equal(g31,g35)
    c: Equal(g18,g32)
    c: Equal(g18,g24)
    c: Distance(g-1,g34) = 7.2
    c: Distance(g-1,g26) = 7.2
    c: Distance(g-1,g30) = 7.2
    c: Distance(g-1,g18) = 13.2
    c: Distance(g-1,g22) = 13.2
    c: Radius(g44) = 2.5
    c: Distance(g-1,g40) = 17.5
    c: Coincident(g9,g39)
    c: PointOnObject(g40,g8)
    c: DistanceX(g-2,g39) = 2.5
FEATURE [PartDesign::Pocket] Pocket005  label="Lid Cutouts"
  BaseFeature = -> BaseFeature001
  Length = 5
  Length2 = 100
  Profile = -> Sketch011
  Type = 0
FEATURE [Sketcher::SketchObject] Sketch012  label="Switch-Lid Indent Sketch"
  FullyConstrained = false
  MapMode = 5
  Placement = pos=(0,0,9) rot=(1,0,0;3.14159rad)
  Support = -> [Pocket005]
  sketch-geometry (8):
    g0: LineSegment StartX=-20.8484 StartY=1.12147 StartZ=0 EndX=-15.2184 EndY=1.12147 EndZ=0
    g1: LineSegment StartX=-15.2184 StartY=1.12147 StartZ=0 EndX=-15.2184 EndY=-15.7685 EndZ=0
    g2: LineSegment StartX=-15.2184 StartY=-15.7685 StartZ=0 EndX=-20.8484 EndY=-15.7685 EndZ=0
    g3: LineSegment StartX=-20.8484 StartY=-15.7685 StartZ=0 EndX=-20.8484 EndY=1.12147 EndZ=0
    g4: LineSegment StartX=1.95221 StartY=-11.0754 StartZ=0 EndX=15.1288 EndY=-11.0754 EndZ=0
    g5: LineSegment StartX=15.1288 StartY=-11.0754 StartZ=0 EndX=15.1288 EndY=-18.1428 EndZ=0
    g6: LineSegment StartX=15.1288 StartY=-18.1428 StartZ=0 EndX=1.95221 EndY=-18.1428 EndZ=0
    g7: LineSegment StartX=1.95221 StartY=-18.1428 StartZ=0 EndX=1.95221 EndY=-11.0754 EndZ=0
  constraints (16):
    c: Coincident(g0,g1)
    c: Coincident(g1,g2)
    c: Coincident(g2,g3)
    c: Coincident(g3,g0)
    c: Horizontal(g0)
    c: Horizontal(g2)
    c: Vertical(g1)
    c: Vertical(g3)
    c: Coincident(g4,g5)
    c: Coincident(g5,g6)
    c: Coincident(g6,g7)
    c: Coincident(g7,g4)
    c: Horizontal(g4)
    c: Horizontal(g6)
    c: Vertical(g5)
    c: Vertical(g7)
FEATURE [PartDesign::Pocket] Pocket006  label="Switch-Lid Indents"
  BaseFeature = -> Pocket005
  Length = 0.5
  Length2 = 100
  Placement = pos=(0,0,80) rot=(0,0,1;0rad)
  Profile = -> Sketch012
  Type = 0
FEATURE [PartDesign::Body] Body004  label="Lid Pocketed"
  BaseFeature = -> Cut
  Group = -> [BaseFeature001,Sketch011,Pocket005,Sketch012,Pocket006]
  Origin = -> Origin004
  Tip = -> Pocket006
COMPONENT P5 — recipe-attached ("Voltage Switch", modeled in this document).
Construction recipe (the document's own serialized feature program — sketch geometry with constraints, then the solid features built on it; lengths are millimeters unless a unit is written):

FEATURE [Sketcher::SketchObject] Sketch013
  AttachmentOffset = pos=(0,0,6) rot=(0,0,1;0rad)
  FullyConstrained = false
  MapMode = 5
  Placement = pos=(0,0,6) rot=(0,0,1;0rad)
  Support = -> [XY_Plane005]
  sketch-geometry (12):
    g0: LineSegment StartX=-20.1185 StartY=14.8189 StartZ=0 EndX=-23.3185 EndY=14.8189 EndZ=0
    g1: LineSegment StartX=-23.3185 StartY=14.8189 StartZ=0 EndX=-23.3185 EndY=9.81891 EndZ=0
    g2: LineSegment StartX=-23.3185 StartY=9.81891 StartZ=0 EndX=-27.3185 EndY=9.81891 EndZ=0
    g3: LineSegment StartX=-27.3185 StartY=9.81891 StartZ=0 EndX=-27.3185 EndY=6.81891 EndZ=0
    g4: LineSegment StartX=-27.3185 StartY=6.81891 StartZ=0 EndX=-23.3185 EndY=6.81891 EndZ=0
    g5: LineSegment StartX=-23.3185 StartY=6.81891 StartZ=0 EndX=-23.3185 EndY=1.81891 EndZ=0
    g6: LineSegment StartX=-23.3185 StartY=1.81891 StartZ=0 EndX=-20.1185 EndY=1.81891 EndZ=0
    g7: LineSegment StartX=-20.1185 StartY=14.8189 StartZ=0 EndX=-20.1185 EndY=9.41668 EndZ=0
    g8: LineSegment StartX=-20.1185 StartY=9.41668 StartZ=0 EndX=-22.1185 EndY=9.41668 EndZ=0
    g9: LineSegment StartX=-22.1185 StartY=9.41668 StartZ=0 EndX=-22.1185 EndY=7.41668 EndZ=0
    g10: LineSegment StartX=-22.1185 StartY=7.41668 StartZ=0 EndX=-20.1185 EndY=7.41668 EndZ=0
    g11: LineSegment StartX=-20.1185 StartY=7.41668 StartZ=0 EndX=-20.1185 EndY=1.81891 EndZ=0
  constraints (32):
    c: Horizontal(g0)
    c: Vertical(g1)
    c: Horizontal(g2)
    c: Vertical(g3)
    c: Coincident(g4,g3)
    c: Horizontal(g4)
    c: Coincident(g5,g4)
    c: Vertical(g5)
    c: Distance(g5) = 5
    c: Distance(g3) = 3
    c: Coincident(g2,g3)
    c: Coincident(g2,g1)
    c: Coincident(g1,g0)
    c: Distance(g2) = 4
    c: Equal(g4,g2)
    c: Equal(g1,g5)
    c: Distance(g0) = 3.2
    c: Coincident(g6,g5)
    c: Horizontal(g6)
    c: Equal(g0,g6)
    c: Coincident(g7,g0)
    c: Coincident(g11,g6)
    c: Horizontal(g8)
    c: Coincident(g9,g8)
    c: Vertical(g9)
    c: Coincident(g10,g9)
    c: Horizontal(g10)
    c: Distance(g9) = 2
    c: Distance(g8) = 2
    c: Coincident(g7,g8)
    c: Coincident(g11,g10)
    c: Tangent(g7,g11)
FEATURE [PartDesign::Pad] Pad006
  Direction = (1,1,1)
  Length = 3.5
  Length2 = 100
  Profile = -> Sketch013
  Type = 0
FEATURE [Sketcher::SketchObject] Sketch014
  FullyConstrained = false
  MapMode = 5
  Placement = pos=(0,0,6) rot=(1,0,0;3.14159rad)
  Support = -> [Pad006]
  sketch-geometry (4):
    g0: LineSegment StartX=-28.4795 StartY=-6.15007 StartZ=0 EndX=-23.3232 EndY=-6.15007 EndZ=0
    g1: LineSegment StartX=-23.3232 StartY=-6.15007 StartZ=0 EndX=-23.3232 EndY=-10.6713 EndZ=0
    g2: LineSegment StartX=-23.3232 StartY=-10.6713 StartZ=0 EndX=-28.4795 EndY=-10.6713 EndZ=0
    g3: LineSegment StartX=-28.4795 StartY=-10.6713 StartZ=0 EndX=-28.4795 EndY=-6.15007 EndZ=0
  constraints (8):
    c: Coincident(g0,g1)
    c: Coincident(g1,g2)
    c: Coincident(g2,g3)
    c: Coincident(g3,g0)
    c: Horizontal(g0)
    c: Horizontal(g2)
    c: Vertical(g1)
    c: Vertical(g3)
FEATURE [PartDesign::Pocket] Pocket007
  BaseFeature = -> Pad006
  Length = 0.8
  Length2 = 100
  Placement = pos=(0,0,50) rot=(0,0,1;0rad)
  Profile = -> Sketch014
  Type = 0
FEATURE [PartDesign::Body] Body005  label="Voltage Switch"
  Group = -> [Sketch013,Pad006,Sketch014,Pocket007]
  Origin = -> Origin005
  Placement = pos=(0,0,-0.4) rot=(0,0,1;0rad)
  Tip = -> Pocket007
COMPONENT P6 — recipe-attached ("JTAG Switch", modeled in this document).
Construction recipe (the document's own serialized feature program — sketch geometry with constraints, then the solid features built on it; lengths are millimeters unless a unit is written):

FEATURE [Sketcher::SketchObject] Sketch015  label="Switch BaseSketch"
  AttachmentOffset = pos=(0,0,13) rot=(0,0,1;0rad)
  FullyConstrained = false
  MapMode = 5
  Placement = pos=(0,0,13) rot=(0,0,1;0rad)
  Support = -> [XY_Plane006]
  sketch-geometry (4):
    g0: LineSegment StartX=4.0378 StartY=17.7452 StartZ=0 EndX=14.9698 EndY=17.7452 EndZ=0
    g1: LineSegment StartX=14.9698 StartY=17.7452 StartZ=0 EndX=14.9698 EndY=11.1067 EndZ=0
    g2: LineSegment StartX=14.9698 StartY=11.1067 StartZ=0 EndX=4.0378 EndY=11.1067 EndZ=0
    g3: LineSegment StartX=4.0378 StartY=11.1067 StartZ=0 EndX=4.0378 EndY=17.7452 EndZ=0
  constraints (8):
    c: Coincident(g0,g1)
    c: Coincident(g1,g2)
    c: Coincident(g2,g3)
    c: Coincident(g3,g0)
    c: Horizontal(g0)
    c: Horizontal(g2)
    c: Vertical(g1)
    c: Vertical(g3)
FEATURE [PartDesign::Pad] Pad007  label="Switch Base"
  Direction = (1,1,1)
  Length = 0.4
  Length2 = 100
  Profile = -> Sketch015
  Type = 0
FEATURE [Sketcher::SketchObject] Sketch016  label="Switch Piller Sketch"
  FullyConstrained = false
  MapMode = 5
  Placement = pos=(0,0,13.4) rot=(0,0,1;0rad)
  Support = -> [Pad007]
  sketch-geometry (4):
    g0: LineSegment StartX=8.41538 StartY=16.209 StartZ=0 EndX=11.9154 EndY=16.209 EndZ=0
    g1: LineSegment StartX=11.9154 StartY=16.209 StartZ=0 EndX=11.9154 EndY=12.709 EndZ=0
    g2: LineSegment StartX=11.9154 StartY=12.709 StartZ=0 EndX=8.41538 EndY=12.709 EndZ=0
    g3: LineSegment StartX=8.41538 StartY=12.709 StartZ=0 EndX=8.41538 EndY=16.209 EndZ=0
  constraints (10):
    c: Coincident(g0,g1)
    c: Coincident(g1,g2)
    c: Coincident(g2,g3)
    c: Coincident(g3,g0)
    c: Horizontal(g0)
    c: Horizontal(g2)
    c: Vertical(g1)
    c: Vertical(g3)
    c: Distance(g1) = 3.5
    c: Distance(g0) = 3.5
FEATURE [PartDesign::Pad] Pad008  label="Switch Pillar"
  BaseFeature = -> Pad007
  Direction = (1,1,1)
  Length = 4
  Length2 = 100
  Profile = -> Sketch016
  Type = 0
FEATURE [Sketcher::SketchObject] Sketch017  label="Switch Hole Sketch"
  FullyConstrained = false
  MapMode = 5
  Placement = pos=(0,0,13) rot=(1,0,0;3.14159rad)
  Support = -> [Pad008]
  sketch-geometry (4):
    g0: LineSegment StartX=9.13506 StartY=-13.4023 StartZ=0 EndX=11.1351 EndY=-13.4023 EndZ=0
    g1: LineSegment StartX=11.1351 StartY=-13.4023 StartZ=0 EndX=11.1351 EndY=-15.4023 EndZ=0
    g2: LineSegment StartX=11.1351 StartY=-15.4023 StartZ=0 EndX=9.13506 EndY=-15.4023 EndZ=0
    g3: LineSegment StartX=9.13506 StartY=-15.4023 StartZ=0 EndX=9.13506 EndY=-13.4023 EndZ=0
  constraints (10):
    c: Coincident(g0,g1)
    c: Coincident(g1,g2)
    c: Coincident(g2,g3)
    c: Coincident(g3,g0)
    c: Horizontal(g0)
    c: Horizontal(g2)
    c: Vertical(g1)
    c: Vertical(g3)
    c: Distance(g0) = 2
    c: Distance(g1) = 2
FEATURE [PartDesign::Pocket] Pocket008  label="Switch Hole"
  BaseFeature = -> Pad008
  Length = 3
  Length2 = 100
  Placement = pos=(0,0,20) rot=(0,0,1;0rad)
  Profile = -> Sketch017
  Type = 0
FEATURE [PartDesign::Body] Body006  label="JTAG Switch"
  Group = -> [Sketch015,Pad007,Sketch016,Pad008,Sketch017,Pocket008]
  Origin = -> Origin006
  Placement = pos=(0,0,-4) rot=(0,0,1;0rad)
  Tip = -> Pocket008
COMPONENT P7 — recipe-attached ("Shim1", modeled in this document).
Construction recipe (the document's own serialized feature program — sketch geometry with constraints, then the solid features built on it; lengths are millimeters unless a unit is written):

FEATURE [Sketcher::SketchObject] Sketch018  label="Shim Sketch"
  AttachmentOffset = pos=(0,0,4.5) rot=(0,0,1;0rad)
  FullyConstrained = true
  MapMode = 5
  Placement = pos=(0,0,4.5) rot=(0,0,1;0rad)
  Support = -> [XY_Plane007]
  sketch-geometry (1):
    g0: Circle CenterX=-20 CenterY=20 CenterZ=0 NormalX=0 NormalY=0 NormalZ=1 AngleXU=0 Radius=2.5
  constraints (3):
    c: DistanceX(g-2,g0) = -20
    c: DistanceY(g-1,g0) = 20
    c: Radius(g0) = 2.5
FEATURE [PartDesign::Pad] Pad009  label="Shim1Pad"
  Direction = (1,1,1)
  Length = 4
  Length2 = 100
  Profile = -> Sketch018
  Type = 0
FEATURE [Sketcher::SketchObject] Sketch019  label="Shim Hole Sketch"
  FullyConstrained = true
  MapMode = 5
  Placement = pos=(0,0,8.5) rot=(0,0,1;0rad)
  Support = -> [Pad009]
  sketch-geometry (1):
    g0: Circle CenterX=-20 CenterY=20 CenterZ=0 NormalX=0 NormalY=0 NormalZ=1 AngleXU=0 Radius=1.75
  constraints (3):
    c: DistanceX(g-2,g0) = -20
    c: DistanceY(g-1,g0) = 20
    c: Radius(g0) = 1.75
FEATURE [PartDesign::Pocket] Pocket009  label="Shim1Pocket"
  BaseFeature = -> Pad009
  Length = 5
  Length2 = 100
  Placement = pos=(-6.93e-14,-7.11e-14,50) rot=(0,0,1;0rad)
  Profile = -> Sketch019
  Type = 1
FEATURE [PartDesign::Body] Body007  label="Shim1"
  Group = -> [Sketch018,Pad009,Sketch019,Pocket009]
  Origin = -> Origin007
  Placement = pos=(0,0,0.7) rot=(0,0,1;0rad)
  Tip = -> Pocket009
COMPONENT P8 — recipe-attached ("Shim2", modeled in this document).
Construction recipe (the document's own serialized feature program — sketch geometry with constraints, then the solid features built on it; lengths are millimeters unless a unit is written):

FEATURE [Sketcher::SketchObject] Sketch020  label="Shim Sketch001"
  AttachmentOffset = pos=(0,0,4.5) rot=(0,0,1;0rad)
  FullyConstrained = true
  MapMode = 5
  Placement = pos=(0,0,4.5) rot=(0,0,1;0rad)
  Support = -> [XY_Plane008]
  sketch-geometry (1):
    g0: Circle CenterX=-20 CenterY=20 CenterZ=0 NormalX=0 NormalY=0 NormalZ=1 AngleXU=0 Radius=2.5
  constraints (3):
    c: DistanceX(g-2,g0) = -20
    c: DistanceY(g-1,g0) = 20
    c: Radius(g0) = 2.5
FEATURE [PartDesign::Pad] Pad010  label="Shim2Pad"
  Direction = (1,1,1)
  Length = 4
  Length2 = 100
  Profile = -> Sketch020
  Type = 0
FEATURE [Sketcher::SketchObject] Sketch021  label="Shim Hole Sketch001"
  FullyConstrained = true
  MapMode = 5
  Placement = pos=(0,0,8.5) rot=(0,0,1;0rad)
  Support = -> [Pad010]
  sketch-geometry (1):
    g0: Circle CenterX=-20 CenterY=20 CenterZ=0 NormalX=0 NormalY=0 NormalZ=1 AngleXU=0 Radius=1.75
  constraints (3):
    c: DistanceX(g-2,g0) = -20
    c: DistanceY(g-1,g0) = 20
    c: Radius(g0) = 1.75
FEATURE [PartDesign::Pocket] Pocket010  label="Shim2Pocket"
  BaseFeature = -> Pad010
  Length = 5
  Length2 = 100
  Placement = pos=(-6.93e-14,-7.11e-14,50) rot=(0,0,1;0rad)
  Profile = -> Sketch021
  Type = 1
FEATURE [PartDesign::Body] Body008  label="Shim2"
  Group = -> [Sketch020,Pad010,Sketch021,Pocket010]
  Origin = -> Origin008
  Placement = pos=(0,0,0.7) rot=(0,0,1;1.5708rad)
  Tip = -> Pocket010
COMPONENT P9 — recipe-attached ("Shim3", modeled in this document).
Construction recipe (the document's own serialized feature program — sketch geometry with constraints, then the solid features built on it; lengths are millimeters unless a unit is written):

FEATURE [Sketcher::SketchObject] Sketch023  label="Shim Sketch002"
  AttachmentOffset = pos=(0,0,4.5) rot=(0,0,1;0rad)
  FullyConstrained = true
  MapMode = 5
  Placement = pos=(0,0,4.5) rot=(0,0,1;0rad)
  Support = -> [XY_Plane009]
  sketch-geometry (1):
    g0: Circle CenterX=-20 CenterY=20 CenterZ=0 NormalX=0 NormalY=0 NormalZ=1 AngleXU=0 Radius=2.5
  constraints (3):
    c: DistanceX(g-2,g0) = -20
    c: DistanceY(g-1,g0) = 20
    c: Radius(g0) = 2.5
FEATURE [PartDesign::Pad] Pad011  label="Shim3Pad"
  Direction = (1,1,1)
  Length = 4
  Length2 = 100
  Profile = -> Sketch023
  Type = 0
FEATURE [Sketcher::SketchObject] Sketch022  label="Shim Hole Sketch002"
  FullyConstrained = true
  MapMode = 5
  Placement = pos=(0,0,8.5) rot=(0,0,1;0rad)
  Support = -> [Pad011]
  sketch-geometry (1):
    g0: Circle CenterX=-20 CenterY=20 CenterZ=0 NormalX=0 NormalY=0 NormalZ=1 AngleXU=0 Radius=1.75
  constraints (3):
    c: DistanceX(g-2,g0) = -20
    c: DistanceY(g-1,g0) = 20
    c: Radius(g0) = 1.75
FEATURE [PartDesign::Pocket] Pocket011  label="Shim3Pocket"
  BaseFeature = -> Pad011
  Length = 5
  Length2 = 100
  Placement = pos=(-6.93e-14,-7.11e-14,50) rot=(0,0,1;0rad)
  Profile = -> Sketch022
  Type = 1
FEATURE [PartDesign::Body] Body009  label="Shim3"
  Group = -> [Sketch023,Pad011,Sketch022,Pocket011]
  Origin = -> Origin009
  Placement = pos=(0,0,0.7) rot=(0,0,1;3.14159rad)
  Tip = -> Pocket011
COMPONENT P10 — recipe-attached ("Shim4", modeled in this document).
Construction recipe (the document's own serialized feature program — sketch geometry with constraints, then the solid features built on it; lengths are millimeters unless a unit is written):

FEATURE [Sketcher::SketchObject] Sketch024  label="Shim Sketch003"
  AttachmentOffset = pos=(0,0,4.5) rot=(0,0,1;0rad)
  FullyConstrained = true
  MapMode = 5
  Placement = pos=(0,0,4.5) rot=(0,0,1;0rad)
  Support = -> [XY_Plane010]
  sketch-geometry (1):
    g0: Circle CenterX=-20 CenterY=20 CenterZ=0 NormalX=0 NormalY=0 NormalZ=1 AngleXU=0 Radius=2.5
  constraints (3):
    c: DistanceX(g-2,g0) = -20
    c: DistanceY(g-1,g0) = 20
    c: Radius(g0) = 2.5
FEATURE [PartDesign::Pad] Pad012  label="Shim4Pad"
  Direction = (1,1,1)
  Length = 4
  Length2 = 100
  Profile = -> Sketch024
  Type = 0
FEATURE [Sketcher::SketchObject] Sketch025  label="Shim Hole Sketch003"
  FullyConstrained = true
  MapMode = 5
  Placement = pos=(0,0,8.5) rot=(0,0,1;0rad)
  Support = -> [Pad012]
  sketch-geometry (1):
    g0: Circle CenterX=-20 CenterY=20 CenterZ=0 NormalX=0 NormalY=0 NormalZ=1 AngleXU=0 Radius=1.75
  constraints (3):
    c: DistanceX(g-2,g0) = -20
    c: DistanceY(g-1,g0) = 20
    c: Radius(g0) = 1.75
FEATURE [PartDesign::Pocket] Pocket012  label="Shim4Pocket"
  BaseFeature = -> Pad012
  Length = 5
  Length2 = 100
  Placement = pos=(-6.93e-14,-7.11e-14,50) rot=(0,0,1;0rad)
  Profile = -> Sketch025
  Type = 1
FEATURE [PartDesign::Body] Body010  label="Shim4"
  Group = -> [Sketch024,Pad012,Sketch025,Pocket012]
  Origin = -> Origin010
  Placement = pos=(0,0,0.7) rot=(0,0,-1;1.5708rad)
  Tip = -> Pocket012
COMPONENT P11 — geometry summary ("C1_C_0402_1005Metric_5EEC7CD1"; no construction recipe available for this part):
  bounding box: 1.0 x 0.5 x 0.5 mm
  tessellated surface: 188 triangles
  volume: 0 mm^3 (91% of its bounding box)
  symmetry: 2-fold rotationally symmetric about the y axis; mirror-symmetric across its y mid-plane, z mid-plane
COMPONENT P12 — geometry summary ("C2_C_0402_1005Metric_5EEC7881"; no construction recipe available for this part):
  bounding box: 1.0 x 0.5 x 0.5 mm
  tessellated surface: 188 triangles
  volume: 0 mm^3 (91% of its bounding box)
  symmetry: 2-fold rotationally symmetric about the y axis; mirror-symmetric across its y mid-plane, z mid-plane
COMPONENT P13 — geometry summary ("C3_C_0402_1005Metric_5EEC8DF3"; no construction recipe available for this part):
  bounding box: 1.0 x 0.5 x 0.5 mm
  tessellated surface: 188 triangles
  volume: 0 mm^3 (91% of its bounding box)
  symmetry: 2-fold rotationally symmetric about the y axis; mirror-symmetric across its y mid-plane, z mid-plane
COMPONENT P14 — geometry summary ("C4_C_0402_1005Metric_5EEC995A"; no construction recipe available for this part):
  bounding box: 1.0 x 0.5 x 0.5 mm
  tessellated surface: 188 triangles
  volume: 0 mm^3 (91% of its bounding box)
  symmetry: 2-fold rotationally symmetric about the y axis; mirror-symmetric across its y mid-plane, z mid-plane
COMPONENT P15 — geometry summary ("C5_C_0402_1005Metric_5EEC9444"; no construction recipe available for this part):
  bounding box: 1.0 x 0.5 x 0.5 mm
  tessellated surface: 188 triangles
  volume: 0 mm^3 (91% of its bounding box)
  symmetry: 2-fold rotationally symmetric about the y axis; mirror-symmetric across its y mid-plane, z mid-plane
COMPONENT P16 — geometry summary ("C6_C_0402_1005Metric_5EEC8FCA"; no construction recipe available for this part):
  bounding box: 1.0 x 0.5 x 0.5 mm
  tessellated surface: 188 triangles
  volume: 0 mm^3 (91% of its bounding box)
  symmetry: 2-fold rotationally symmetric about the y axis; mirror-symmetric across its y mid-plane, z mid-plane
COMPONENT P17 — geometry summary ("C7_C_0402_1005Metric_5EEC954C"; no construction recipe available for this part):
  bounding box: 1.0 x 0.5 x 0.5 mm
  tessellated surface: 188 triangles
  volume: 0 mm^3 (91% of its bounding box)
  symmetry: 2-fold rotationally symmetric about the y axis; mirror-symmetric across its y mid-plane, z mid-plane
COMPONENT P18 — geometry summary ("C8_C_0402_1005Metric_5EEC96B4"; no construction recipe available for this part):
  bounding box: 1.0 x 0.5 x 0.5 mm
  tessellated surface: 188 triangles
  volume: 0 mm^3 (91% of its bounding box)
  symmetry: 2-fold rotationally symmetric about the y axis; mirror-symmetric across its y mid-plane, z mid-plane
COMPONENT P19 — geometry summary ("C9_C_0402_1005Metric_5EEC89A9"; no construction recipe available for this part):
  bounding box: 1.0 x 0.5 x 0.5 mm
  tessellated surface: 188 triangles
  volume: 0 mm^3 (91% of its bounding box)
  symmetry: 2-fold rotationally symmetric about the y axis; mirror-symmetric across its y mid-plane, z mid-plane
COMPONENT P20 — geometry summary ("C10_C_0402_1005Metric_5EEC9930"; no construction recipe available for this part):
  bounding box: 1.0 x 0.5 x 0.5 mm
  tessellated surface: 188 triangles
  volume: 0 mm^3 (91% of its bounding box)
  symmetry: 2-fold rotationally symmetric about the y axis; mirror-symmetric across its y mid-plane, z mid-plane
COMPONENT P21 — geometry summary ("C11_C_0402_1005Metric_5EEC82B6"; no construction recipe available for this part):
  bounding box: 1.0 x 0.5 x 0.5 mm
  tessellated surface: 188 triangles
  volume: 0 mm^3 (91% of its bounding box)
  symmetry: 2-fold rotationally symmetric about the y axis; mirror-symmetric across its y mid-plane, z mid-plane
COMPONENT P22 — geometry summary ("C12_C_0402_1005Metric_5EEC79C5"; no construction recipe available for this part):
  bounding box: 1.0 x 0.5 x 0.5 mm
  tessellated surface: 188 triangles
  volume: 0 mm^3 (91% of its bounding box)
  symmetry: 2-fold rotationally symmetric about the y axis; mirror-symmetric across its y mid-plane, z mid-plane
COMPONENT P23 — geometry summary ("C13_C_0402_1005Metric_5EEC989A"; no construction recipe available for this part):
  bounding box: 1.0 x 0.5 x 0.5 mm
  tessellated surface: 188 triangles
  volume: 0 mm^3 (91% of its bounding box)
  symmetry: 2-fold rotationally symmetric about the y axis; mirror-symmetric across its y mid-plane, z mid-plane
COMPONENT P24 — geometry summary ("C14_C_0402_1005Metric_5EEC8136"; no construction recipe available for this part):
  bounding box: 1.0 x 0.5 x 0.5 mm
  tessellated surface: 188 triangles
  volume: 0 mm^3 (91% of its bounding box)
  symmetry: 2-fold rotationally symmetric about the y axis; mirror-symmetric across its y mid-plane, z mid-plane
COMPONENT P25 — geometry summary ("C15_C_0402_1005Metric_5EEC97C2"; no construction recipe available for this part):
  bounding box: 1.0 x 0.5 x 0.5 mm
  tessellated surface: 188 triangles
  volume: 0 mm^3 (91% of its bounding box)
  symmetry: 2-fold rotationally symmetric about the y axis; mirror-symmetric across its y mid-plane, z mid-plane
COMPONENT P26 — geometry summary ("C17_C_0402_1005Metric_5EEC8FF4"; no construction recipe available for this part):
  bounding box: 1.0 x 0.5 x 0.5 mm
  tessellated surface: 188 triangles
  volume: 0 mm^3 (91% of its bounding box)
  symmetry: 2-fold rotationally symmetric about the y axis; mirror-symmetric across its y mid-plane, z mid-plane
COMPONENT P27 — geometry summary ("C18_C_0402_1005Metric_5EEC8F76"; no construction recipe available for this part):
  bounding box: 1.0 x 0.5 x 0.5 mm
  tessellated surface: 188 triangles
  volume: 0 mm^3 (91% of its bounding box)
  symmetry: 2-fold rotationally symmetric about the y axis; mirror-symmetric across its y mid-plane, z mid-plane
COMPONENT P28 — geometry summary ("C19_C_0402_1005Metric_5EEC8E47"; no construction recipe available for this part):
  bounding box: 1.0 x 0.5 x 0.5 mm
  tessellated surface: 188 triangles
  volume: 0 mm^3 (91% of its bounding box)
  symmetry: 2-fold rotationally symmetric about the y axis; mirror-symmetric across its y mid-plane, z mid-plane
COMPONENT P29 — geometry summary ("C20_C_0402_1005Metric_5EEC935D"; no construction recipe available for this part):
  bounding box: 1.0 x 0.5 x 0.5 mm
  tessellated surface: 188 triangles
  volume: 0 mm^3 (91% of its bounding box)
  symmetry: 2-fold rotationally symmetric about the y axis; mirror-symmetric across its y mid-plane, z mid-plane
COMPONENT P30 — geometry summary ("C21_C_0402_1005Metric_5EEC9D08"; no construction recipe available for this part):
  bounding box: 1.0 x 0.5 x 0.5 mm
  tessellated surface: 188 triangles
  volume: 0 mm^3 (91% of its bounding box)
  symmetry: 2-fold rotationally symmetric about the y axis; mirror-symmetric across its y mid-plane, z mid-plane
COMPONENT P31 — geometry summary ("C22_C_0402_1005Metric_5EEC9C33"; no construction recipe available for this part):
  bounding box: 1.0 x 0.5 x 0.5 mm
  tessellated surface: 188 triangles
  volume: 0 mm^3 (91% of its bounding box)
  symmetry: 2-fold rotationally symmetric about the y axis; mirror-symmetric across its y mid-plane, z mid-plane
COMPONENT P32 — geometry summary ("C23_C_0402_1005Metric_5EEC8AB1"; no construction recipe available for this part):
  bounding box: 1.0 x 0.5 x 0.5 mm
  tessellated surface: 188 triangles
  volume: 0 mm^3 (91% of its bounding box)
  symmetry: 2-fold rotationally symmetric about the y axis; mirror-symmetric across its y mid-plane, z mid-plane
COMPONENT P33 — geometry summary ("C24_C_0402_1005Metric_5EEC9C5D"; no construction recipe available for this part):
  bounding box: 1.0 x 0.5 x 0.5 mm
  tessellated surface: 188 triangles
  volume: 0 mm^3 (91% of its bounding box)
  symmetry: 2-fold rotationally symmetric about the y axis; mirror-symmetric across its y mid-plane, z mid-plane
COMPONENT P34 — geometry summary ("C25_C_0402_1005Metric_5EEC78D5"; no construction recipe available for this part):
  bounding box: 1.0 x 0.5 x 0.5 mm
  tessellated surface: 188 triangles
  volume: 0 mm^3 (91% of its bounding box)
  symmetry: 2-fold rotationally symmetric about the y axis; mirror-symmetric across its y mid-plane, z mid-plane
COMPONENT P35 — geometry summary ("C26_C_0402_1005Metric_5EEC78AB"; no construction recipe available for this part):
  bounding box: 1.0 x 0.5 x 0.5 mm
  tessellated surface: 188 triangles
  volume: 0 mm^3 (91% of its bounding box)
  symmetry: 2-fold rotationally symmetric about the y axis; mirror-symmetric across its y mid-plane, z mid-plane
COMPONENT P36 — geometry summary ("D2_LED_0603_1608Metric_5EEC7993"; no construction recipe available for this part):
  bounding box: 1.6 x 1.1 x 0.8 mm
  tessellated surface: 232 triangles
  volume: 1 mm^3 (76% of its bounding box)
  symmetry: 2-fold rotationally symmetric about the z axis; mirror-symmetric across its x mid-plane
COMPONENT P37 — geometry summary ("D3_LED_0603_1608Metric_5EEC7843"; no construction recipe available for this part):
  bounding box: 1.6 x 1.1 x 0.8 mm
  tessellated surface: 232 triangles
  volume: 1 mm^3 (76% of its bounding box)
  symmetry: 2-fold rotationally symmetric about the z axis; mirror-symmetric across its x mid-plane
COMPONENT P38 — geometry summary ("D4_LED_0603_1608Metric_5EEC98C8"; no construction recipe available for this part):
  bounding box: 1.6 x 1.1 x 0.8 mm
  tessellated surface: 232 triangles
  volume: 1 mm^3 (76% of its bounding box)
  symmetry: 2-fold rotationally symmetric about the z axis; mirror-symmetric across its x mid-plane
COMPONENT P39 — geometry summary ("D5_LED_0603_1608Metric_5EEC98FE"; no construction recipe available for this part):
  bounding box: 1.6 x 1.1 x 0.8 mm
  tessellated surface: 232 triangles
  volume: 1 mm^3 (76% of its bounding box)
  symmetry: 2-fold rotationally symmetric about the z axis; mirror-symmetric across its x mid-plane
COMPONENT P40 — geometry summary ("FB2_L_0402_1005Metric_5EEC8C9D"; no construction recipe available for this part):
  bounding box: 1.0 x 0.5 x 0.5 mm
  tessellated surface: 188 triangles
  volume: 0 mm^3 (91% of its bounding box)
  symmetry: 4-fold rotationally symmetric about the x axis; mirror-symmetric across its x mid-plane, z mid-plane
COMPONENT P41 — geometry summary ("FB3_L_0402_1005Metric_5EEC83E8"; no construction recipe available for this part):
  bounding box: 1.0 x 0.5 x 0.5 mm
  tessellated surface: 188 triangles
  volume: 0 mm^3 (91% of its bounding box)
  symmetry: 4-fold rotationally symmetric about the x axis; mirror-symmetric across its x mid-plane, z mid-plane
COMPONENT P42 — geometry summary ("R2_R_0402_1005Metric_5EEC8FA0"; no construction recipe available for this part):
  bounding box: 1.0 x 0.5 x 0.3 mm
  tessellated surface: 148 triangles
  volume: 0 mm^3 (93% of its bounding box)
  symmetry: mirror-symmetric across its x mid-plane
COMPONENT P43 — geometry summary ("R4_R_0402_1005Metric_5EEC8A84"; no construction recipe available for this part):
  bounding box: 1.0 x 0.5 x 0.3 mm
  tessellated surface: 148 triangles
  volume: 0 mm^3 (93% of its bounding box)
  symmetry: mirror-symmetric across its x mid-plane
COMPONENT P44 — geometry summary ("R5_R_0402_1005Metric_5EEC897F"; no construction recipe available for this part):
  bounding box: 1.0 x 0.5 x 0.3 mm
  tessellated surface: 148 triangles
  volume: 0 mm^3 (93% of its bounding box)
  symmetry: mirror-symmetric across its x mid-plane
COMPONENT P45 — geometry summary ("R6_R_0402_1005Metric_5EEC916B"; no construction recipe available for this part):
  bounding box: 1.0 x 0.5 x 0.3 mm
  tessellated surface: 148 triangles
  volume: 0 mm^3 (93% of its bounding box)
  symmetry: mirror-symmetric across its x mid-plane
COMPONENT P46 — geometry summary ("R7_R_0402_1005Metric_5EEC9471"; no construction recipe available for this part):
  bounding box: 1.0 x 0.5 x 0.3 mm
  tessellated surface: 148 triangles
  volume: 0 mm^3 (93% of its bounding box)
  symmetry: mirror-symmetric across its x mid-plane
COMPONENT P47 — geometry summary ("R8_R_0402_1005Metric_5EEC94A1"; no construction recipe available for this part):
  bounding box: 1.0 x 0.5 x 0.3 mm
  tessellated surface: 148 triangles
  volume: 0 mm^3 (93% of its bounding box)
  symmetry: mirror-symmetric across its x mid-plane
COMPONENT P48 — geometry summary ("R9_R_0402_1005Metric_5EEC9279"; no construction recipe available for this part):
  bounding box: 1.0 x 0.5 x 0.3 mm
  tessellated surface: 148 triangles
  volume: 0 mm^3 (93% of its bounding box)
  symmetry: mirror-symmetric across its x mid-plane
COMPONENT P49 — geometry summary ("R10_R_0402_1005Metric_5EEC9333"; no construction recipe available for this part):
  bounding box: 1.0 x 0.5 x 0.3 mm
  tessellated surface: 148 triangles
  volume: 0 mm^3 (93% of its bounding box)
  symmetry: mirror-symmetric across its x mid-plane
COMPONENT P50 — geometry summary ("R11_R_0402_1005Metric_5EEC8E1D"; no construction recipe available for this part):
  bounding box: 1.0 x 0.5 x 0.3 mm
  tessellated surface: 148 triangles
  volume: 0 mm^3 (93% of its bounding box)
  symmetry: mirror-symmetric across its x mid-plane
COMPONENT P51 — geometry summary ("R12_R_0402_1005Metric_5EEC8109"; no construction recipe available for this part):
  bounding box: 1.0 x 0.5 x 0.3 mm
  tessellated surface: 148 triangles
  volume: 0 mm^3 (93% of its bounding box)
  symmetry: mirror-symmetric across its x mid-plane
COMPONENT P52 — geometry summary ("R13_R_0402_1005Metric_5EEC8D1E"; no construction recipe available for this part):
  bounding box: 1.0 x 0.5 x 0.3 mm
  tessellated surface: 148 triangles
  volume: 0 mm^3 (93% of its bounding box)
  symmetry: mirror-symmetric across its x mid-plane
COMPONENT P53 — geometry summary ("R14_R_0402_1005Metric_5EEC8394"; no construction recipe available for this part):
  bounding box: 1.0 x 0.5 x 0.3 mm
  tessellated surface: 148 triangles
  volume: 0 mm^3 (93% of its bounding box)
  symmetry: mirror-symmetric across its x mid-plane
COMPONENT P54 — geometry summary ("R15_R_0402_1005Metric_5EEC9309"; no construction recipe available for this part):
  bounding box: 1.0 x 0.5 x 0.3 mm
  tessellated surface: 148 triangles
  volume: 0 mm^3 (93% of its bounding box)
  symmetry: mirror-symmetric across its x mid-plane
COMPONENT P55 — geometry summary ("R16_R_0402_1005Metric_5EEC82E0"; no construction recipe available for this part):
  bounding box: 1.0 x 0.5 x 0.3 mm
  tessellated surface: 148 triangles
  volume: 0 mm^3 (93% of its bounding box)
  symmetry: mirror-symmetric across its x mid-plane
COMPONENT P56 — geometry summary ("R17_R_0402_1005Metric_5EEC9870"; no construction recipe available for this part):
  bounding box: 1.0 x 0.5 x 0.3 mm
  tessellated surface: 148 triangles
  volume: 0 mm^3 (93% of its bounding box)
  symmetry: mirror-symmetric across its x mid-plane
COMPONENT P57 — geometry summary ("R18_R_0402_1005Metric_5EEC9141"; no construction recipe available for this part):
  bounding box: 1.0 x 0.5 x 0.3 mm
  tessellated surface: 148 triangles
  volume: 0 mm^3 (93% of its bounding box)
  symmetry: mirror-symmetric across its x mid-plane
COMPONENT P58 — geometry summary ("R19_R_0402_1005Metric_5EEC8955"; no construction recipe available for this part):
  bounding box: 1.0 x 0.5 x 0.3 mm
  tessellated surface: 148 triangles
  volume: 0 mm^3 (93% of its bounding box)
  symmetry: mirror-symmetric across its x mid-plane
COMPONENT P59 — geometry summary ("R20_R_0402_1005Metric_5EEC8DC9"; no construction recipe available for this part):
  bounding box: 1.0 x 0.5 x 0.3 mm
  tessellated surface: 148 triangles
  volume: 0 mm^3 (93% of its bounding box)
  symmetry: mirror-symmetric across its x mid-plane
COMPONENT P60 — geometry summary ("R21_R_0402_1005Metric_5EEC92DF"; no construction recipe available for this part):
  bounding box: 1.0 x 0.5 x 0.3 mm
  tessellated surface: 148 triangles
  volume: 0 mm^3 (93% of its bounding box)
  symmetry: mirror-symmetric across its x mid-plane
COMPONENT P61 — geometry summary ("R3_R_0402_1005Metric_5EEC83BE"; no construction recipe available for this part):
  bounding box: 1.0 x 0.5 x 0.3 mm
  tessellated surface: 148 triangles
  volume: 0 mm^3 (93% of its bounding box)
  symmetry: mirror-symmetric across its x mid-plane
COMPONENT P62 — geometry summary ("R24_R_0402_1005Metric_5EEC9CDE"; no construction recipe available for this part):
  bounding box: 1.0 x 0.5 x 0.3 mm
  tessellated surface: 148 triangles
  volume: 0 mm^3 (93% of its bounding box)
  symmetry: mirror-symmetric across its x mid-plane
COMPONENT P63 — geometry summary ("R22_R_0402_1005Metric_5F30E668"; no construction recipe available for this part):
  bounding box: 1.0 x 0.5 x 0.3 mm
  tessellated surface: 148 triangles
  volume: 0 mm^3 (93% of its bounding box)
  symmetry: mirror-symmetric across its x mid-plane
COMPONENT P64 — geometry summary ("RN5_R_Array_Convex_4x0402_5EEC8D50"; no construction recipe available for this part):
  bounding box: 2.0 x 1.0 x 0.3 mm
  tessellated surface: 1,640 triangles
  volume: 1 mm^3 (76% of its bounding box)
  symmetry: 2-fold rotationally symmetric about the z axis; mirror-symmetric across its y mid-plane
COMPONENT P65 — geometry summary ("RN6_R_Array_Convex_4x0402_5EEC9836"; no construction recipe available for this part):
  bounding box: 2.0 x 1.0 x 0.3 mm
  tessellated surface: 1,640 triangles
  volume: 1 mm^3 (76% of its bounding box)
  symmetry: 2-fold rotationally symmetric about the z axis; mirror-symmetric across its y mid-plane
COMPONENT P66 — geometry summary ("RN7_R_Array_Convex_4x0402_5EEC950F"; no construction recipe available for this part):
  bounding box: 2.0 x 1.0 x 0.3 mm
  tessellated surface: 1,640 triangles
  volume: 1 mm^3 (76% of its bounding box)
  symmetry: 2-fold rotationally symmetric about the z axis; mirror-symmetric across its y mid-plane
COMPONENT P67 — geometry summary ("RN8_R_Array_Convex_4x0402_5EEC97F4"; no construction recipe available for this part):
  bounding box: 2.0 x 1.0 x 0.3 mm
  tessellated surface: 1,640 triangles
  volume: 1 mm^3 (76% of its bounding box)
  symmetry: 2-fold rotationally symmetric about the z axis; mirror-symmetric across its y mid-plane
COMPONENT P68 — geometry summary ("RN1_R_Array_Convex_4x0402_5EEC8BB2"; no construction recipe available for this part):
  bounding box: 2.0 x 1.0 x 0.3 mm
  tessellated surface: 1,640 triangles
  volume: 1 mm^3 (76% of its bounding box)
  symmetry: 2-fold rotationally symmetric about the z axis; mirror-symmetric across its y mid-plane
COMPONENT P69 — geometry summary ("RN3_R_Array_Convex_4x0402_5EEC8EB5"; no construction recipe available for this part):
  bounding box: 2.0 x 1.0 x 0.3 mm
  tessellated surface: 1,640 triangles
  volume: 1 mm^3 (76% of its bounding box)
  symmetry: 2-fold rotationally symmetric about the z axis; mirror-symmetric across its y mid-plane
COMPONENT P70 — geometry summary ("RN4_R_Array_Convex_4x0402_5EEC8039"; no construction recipe available for this part):
  bounding box: 2.0 x 1.0 x 0.3 mm
  tessellated surface: 1,640 triangles
  volume: 1 mm^3 (76% of its bounding box)
  symmetry: 2-fold rotationally symmetric about the z axis; mirror-symmetric across its y mid-plane
COMPONENT P71 — geometry summary ("U2_SOT_23_5_5EEC94D1"; no construction recipe available for this part):
  bounding box: 2.9 x 2.8 x 1.5 mm
  tessellated surface: 1,176 triangles
  volume: 7 mm^3 (52% of its bounding box)
  symmetry: mirror-symmetric across its y mid-plane
COMPONENT P72 — geometry summary ("U5_TSSOP_24_44x78mm_P065mm_5EEC76EF"; no construction recipe available for this part):
  bounding box: 7.8 x 6.4 x 1.0 mm
  tessellated surface: 5,612 triangles
  volume: 30 mm^3 (62% of its bounding box)
  symmetry: 2-fold rotationally symmetric about the z axis; mirror-symmetric across its x mid-plane
PROVENANCE & LICENSES
A FreeCAD (.FCStd) document from a public repository crawl; recipes are the document's own serialized feature recipes (and, for linked parts, companion documents' recipes).
License: other.
